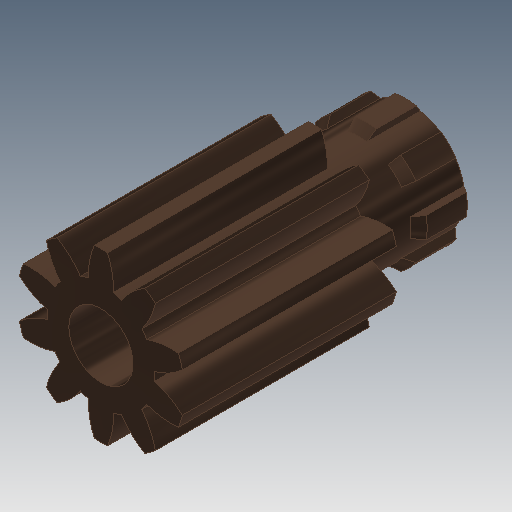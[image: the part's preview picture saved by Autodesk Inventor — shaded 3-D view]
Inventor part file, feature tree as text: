
AUTODESK INVENTOR PART (.ipt)
format: ipt  version: 2017 (Build 210142000, 142)  size: 274,432 bytes
history: native  units: mm (DEFAULTED — no unit token found)
features: sketch x5, extrude x4, plane x3, other x3, chamfer x2, pattern_circular x1, projected_geometry x1
ambient origin geometry x8: Origin, YZ Plane, XZ Plane, XY Plane, X Axis, Y Axis, Z Axis, Center Point
bodies: Solid1 (feature_tree)
feature tree (19):
  extrude  "Extrusion1"  Depth=4.0mm TaperAngle=0.0deg
  plane  "Work Plane2"
  plane  "Work Plane8"
  plane  "Work Plane9"
  other  "Цилиндрическое зубчатое зацепление"
  extrude  "Выдавливание2"  Depth=10.0mm TaperAngle=0.0deg
  extrude  "Выдавливание3"  Depth=1.0mm
  chamfer  "Фаска1"  Distance=3.141593mm
  chamfer  "Фаска2"  [1 undecoded]
  pattern_circular  "Круговой массив1"  [2 undecoded]
  extrude  "Выдавливание4"  Depth=1.0mm
  sketch  "Sketch1"  dims[d0=3.135mm d1=4.0mm d2=0.0mm]
  sketch  "Sketch2"  dims[d3=2.5mm d4=10.0mm d5=0.0mm d16=6.0mm d17=0.0mm d34=3.141593mm d39=0.0mm d41=0.0mm d43=6.0mm d46=6.0mm d47=0.0mm d48=0.0mm d49=2.0mm d50=1.8mm d51=0.0mm d52=0.15mm d53=3.490659mm d54=1.0mm d55=0.0mm d56=0.15mm d57=2.0mm d58=45.0deg d59=0.15mm d60=0.1mm d61=45.0deg d62=80.0mm d63=360.0deg d65=1.2mm d66=6.75mm d67=0.0mm]
  other  "Srf1"
  sketch  "Эскиз3"
  sketch  "Эскиз4"
  projected_geometry  "Спроецированная петля1"
  sketch  "Эскиз5"
  other  "Средний диаметр"
note: 3 required parameter values undecoded (feature->parameter linkage not recoverable at this tier; creation-order binding heuristic only, values carry confidence <= 0.55)
